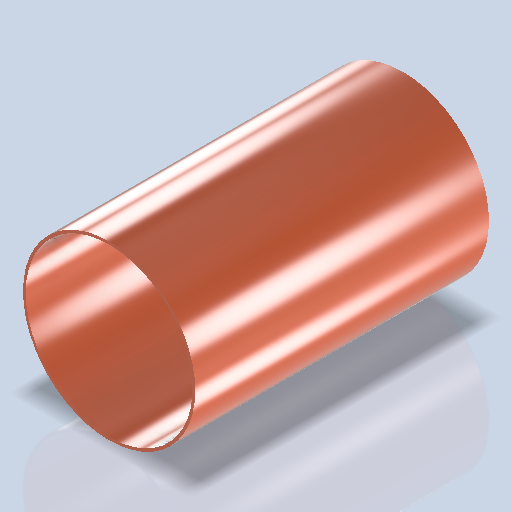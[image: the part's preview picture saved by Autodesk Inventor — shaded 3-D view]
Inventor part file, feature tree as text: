
AUTODESK INVENTOR PART (.ipt)
format: ipt  version: 2024.2 (Build 282272000, 272)  size: 214,016 bytes
history: native  units: mm
features: extrude x1, sketch x1
ambient origin geometry x8: Origin, YZ Plane, XZ Plane, XY Plane, X Axis, Y Axis, Z Axis, Center Point
bodies: Volumenkörper1 (feature_tree)
feature tree (2):
  extrude  "Extrusion1"  Depth=162.0mm
  sketch  "Skizze1"  dims[d0=95.0mm d1=92.0mm d2=162.0mm d3=0.0mm]
